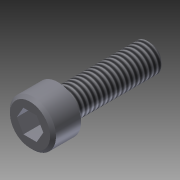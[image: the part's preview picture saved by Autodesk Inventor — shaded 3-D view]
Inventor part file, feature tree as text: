
AUTODESK INVENTOR PART (.ipt)
format: ipt  version: 2011 (Build 150239000, 239)  size: 107,008 bytes
history: native  units: in
note: dims shown in document units (in); Inventor stores cm internally (conversion verified against a paired STEP export)
features: extrude x3, sketch x3, chamfer x2, thread x1
ambient origin geometry x8: Origin, YZ Plane, XZ Plane, XY Plane, X Axis, Y Axis, Z Axis, Center Point
bodies: Solid1 (feature_tree)
feature tree (9):
  extrude  "Extrusion1"  Depth=0.19in TaperAngle=0.0deg
  extrude  "Extrusion2"  Depth=0.625in TaperAngle=0.0deg
  extrude  "Extrusion3"  Depth=0.125in TaperAngle=0.0deg
  thread  "Thread1"  [1 undecoded]
  chamfer  "Chamfer1"  Distance=0.02in Angle=45.0deg
  chamfer  "Chamfer2"  Distance=0.02in Angle=45.0deg
  sketch  "Sketch1"  dims[d0=0.312in d1=0.19in d2=0.0in]
  sketch  "Sketch2"  dims[d3=0.19in d4=0.625in d5=0.0in]
  sketch  "Sketch3"  dims[d6=0.1562in d7=0.125in d8=0.0in d9=1.0in d10=0.0in d11=0.02in d12=0.125in d13=45.0deg d14=0.02in d15=0.125in d16=45.0deg]
note: 1 required parameter value undecoded (feature->parameter linkage not recoverable at this tier; creation-order binding heuristic only, values carry confidence <= 0.55)
